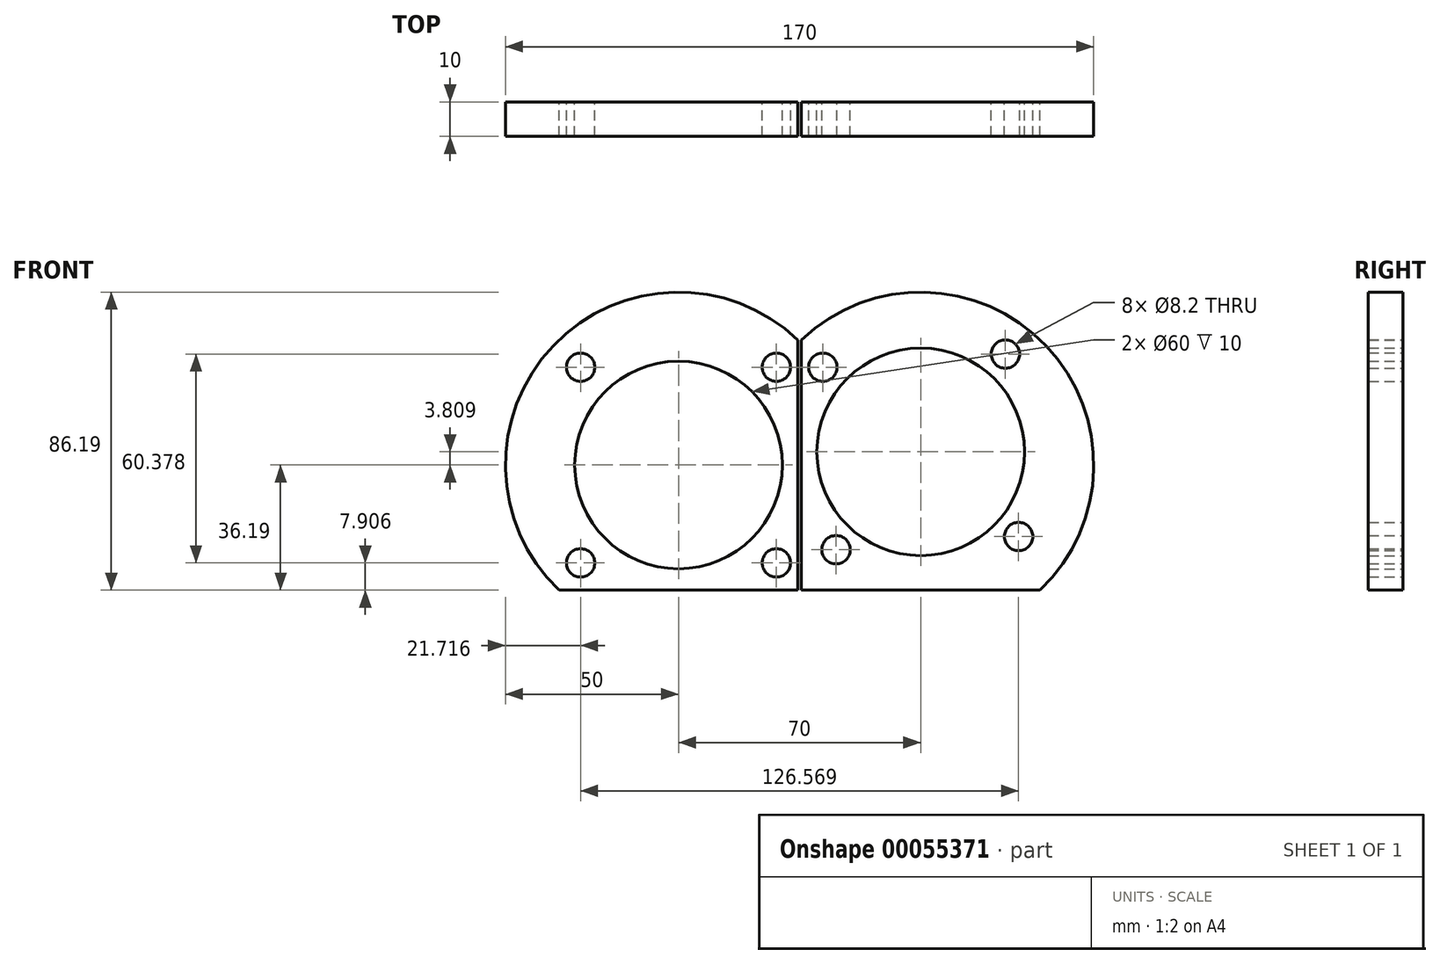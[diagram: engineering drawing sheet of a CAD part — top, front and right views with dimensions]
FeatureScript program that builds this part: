
annotation { "Feature Type Name" : "Feature", "Feature Type Description" : "" }
export const myFeature = defineFeature(function(context is Context, id is Id, definition is map)
    precondition{}
    {
        {
            var Q0;
            Q0=qCreatedBy(makeId("Front.planeOp"),FACE);
            var sketch = newSketch(context, id + "F0", { "sketchPlane" : qUnion([Q0])});
            skCircle(sketch, "E0", {"center": v(-35, 0) * mm, "radius": 30 * mm});
            skArc(sketch, "E1", {"start": v(-0.5, 36.2) * mm, "mid": v(-71.2, 34.5) * mm, "end": v(-69.5, -36.2) * mm});
            skArc(sketch, "E2.trimOffspring", {"start": v(69.5, -36.2) * mm, "mid": v(71.2, 34.5) * mm, "end": v(0.5, 36.2) * mm});
            skCircle(sketch, "E3", {"center": v(35, 3.8) * mm, "radius": 30 * mm});
            skCircle(sketch, "E4.1.0", {"center": v(-63.28, 28.28) * mm, "radius": 4.1 * mm});
            skCircle(sketch, "E4.3.0", {"center": v(-63.28, -28.28) * mm, "radius": 4.1 * mm});
            skCircle(sketch, "E4.5.0", {"center": v(-6.72, -28.28) * mm, "radius": 4.1 * mm});
            skCircle(sketch, "E4.7.0", {"center": v(-6.72, 28.28) * mm, "radius": 4.1 * mm});
            skCircle(sketch, "E5.1.0", {"center": v(6.72, 28.28) * mm, "radius": 4.1 * mm});
            skCircle(sketch, "E6.1.3.0", {"center": v(10.53, -24.47) * mm, "radius": 4.1 * mm});
            skCircle(sketch, "E6.1.5.0", {"center": v(63.28, -20.67) * mm, "radius": 4.1 * mm});
            skCircle(sketch, "E6.1.7.0", {"center": v(59.47, 32.1) * mm, "radius": 4.1 * mm});
            skLineSegment(sketch, "E7.0", {"start": v(-0.5, 36.2) * mm, "end": v(-0.5, -36.2) * mm});
            skLineSegment(sketch, "E8.0", {"start": v(0.5, 36.2) * mm, "end": v(0.5, -36.2) * mm});
            skLineSegment(sketch, "E9", {"start": v(0.5, -36.2) * mm, "end": v(69.5, -36.2) * mm});
            skLineSegment(sketch, "E10", {"start": v(69.5, -36.2) * mm, "end": v(0.5, -36.2) * mm});
            skLineSegment(sketch, "E11.trimOffspring", {"start": v(-0.5, -36.2) * mm, "end": v(-69.5, -36.2) * mm});
            skSolve(sketch);
        }
        {
            var Q0;
            Q0=makeQuery(id+"F0.imprint","IMPRINT",FACE,{"disambiguationData":[TD([[makeQuery(id+"F0.imprint","IMPRINT",EDGE,{"derivedFrom":sQuery(id+"F0.wireOp",EDGE,"E0")}),-1.0]])]});
            var Q1;
            Q1=makeQuery(id+"F0.imprint","IMPRINT",FACE,{"disambiguationData":[TD([[makeQuery(id+"F0.imprint","IMPRINT",EDGE,{"derivedFrom":sQuery(id+"F0.wireOp",EDGE,"E2.trimOffspring")}),1.0]])]});
            extrude(context, id + "F1", {"entities" : qUnion([Q0, Q1]), "depth" : 10 * mm});
        }
    });
